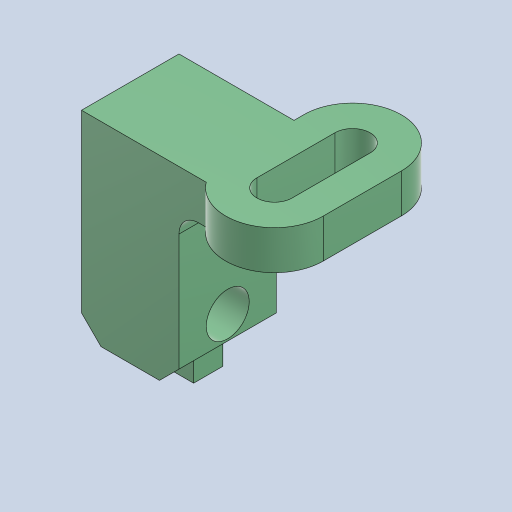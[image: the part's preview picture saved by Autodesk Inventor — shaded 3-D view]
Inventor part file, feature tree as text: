
AUTODESK INVENTOR PART (.ipt)
format: ipt  version: 2023 (Build 270158000, 158)  size: 190,464 bytes
history: native  units: mm
features: sketch x3, extrude x3, other x2, hole x1, fillet x1, chamfer x1
ambient origin geometry x8: Origin, YZ Plane, XZ Plane, XY Plane, X Axis, Y Axis, Z Axis, Center Point
bodies: Body1 (feature_tree)
feature tree (11):
  other  "ソリッド1"
  sketch  "スケッチ1"
  extrude  "押し出し1"  Depth=1.8mm
  extrude  "押し出し4"  Depth=4.0mm
  hole  "穴2"  [1 undecoded]
  fillet  "フィレット2"  Radius=2.0mm
  other  "作業平面2"
  chamfer  "面取り1"  Distance=5.0mm
  extrude  "押し出し5"  Depth=5.9mm
  sketch  "スケッチ5"
  sketch  "スケッチ6"
note: 1 required parameter value undecoded (feature->parameter linkage not recoverable at this tier; creation-order binding heuristic only, values carry confidence <= 0.55)
